# Revit family: TD92_ELO727_SAL220_RVT20_R00
name_source: partatom
category: Mobiliário
units: mm (PartAtom-declared; Revit-internal decimal feet)

## family parameters
Com base no plano de trabalho = Não
Compartilhado = Não
Corte com vazios quando carregada = Não
Número OmniClass = 23.40.20.00
Ponto de cálculo do ambiente = Não
Sempre na vertical = Sim
Título OmniClass = General Furniture and Specialties

## types (1)
- TD92_ELO727_SAL220_RVT20_R00
    Descrição = Forma pura, integração e modernidade no ambiente. O Banco Tramontina Elo em Polietileno é perfeito para ambientar áreas coletivas com bom gosto e design. Atende todas as propostas de decoração, desde as sofisticadas às despojadas. Formas versáteis desenham o Banco Elo, que combina com tudo, inserindo energia aos espaços e conquistando os olhares atentos às tendências. A Casa Delta é uma coleção de móveis e acessórios para personalizar ambientes com estilo e criar espaços que refletem o prazer de viver, o prazer de fazer bonito.
    Elevação padrão = 0  [stored 0 ft]
    Fabricante = Tramontina Delta S/A
    Modelo = Banco Tramontina Elo em Polietileno Sálvia
    Nota-chave = 92727220
    URL = https://www.tramontinastore.com

note: [stored X ft] marks values corroborated as IEEE doubles in the binary element streams (Revit-internal decimal feet)
